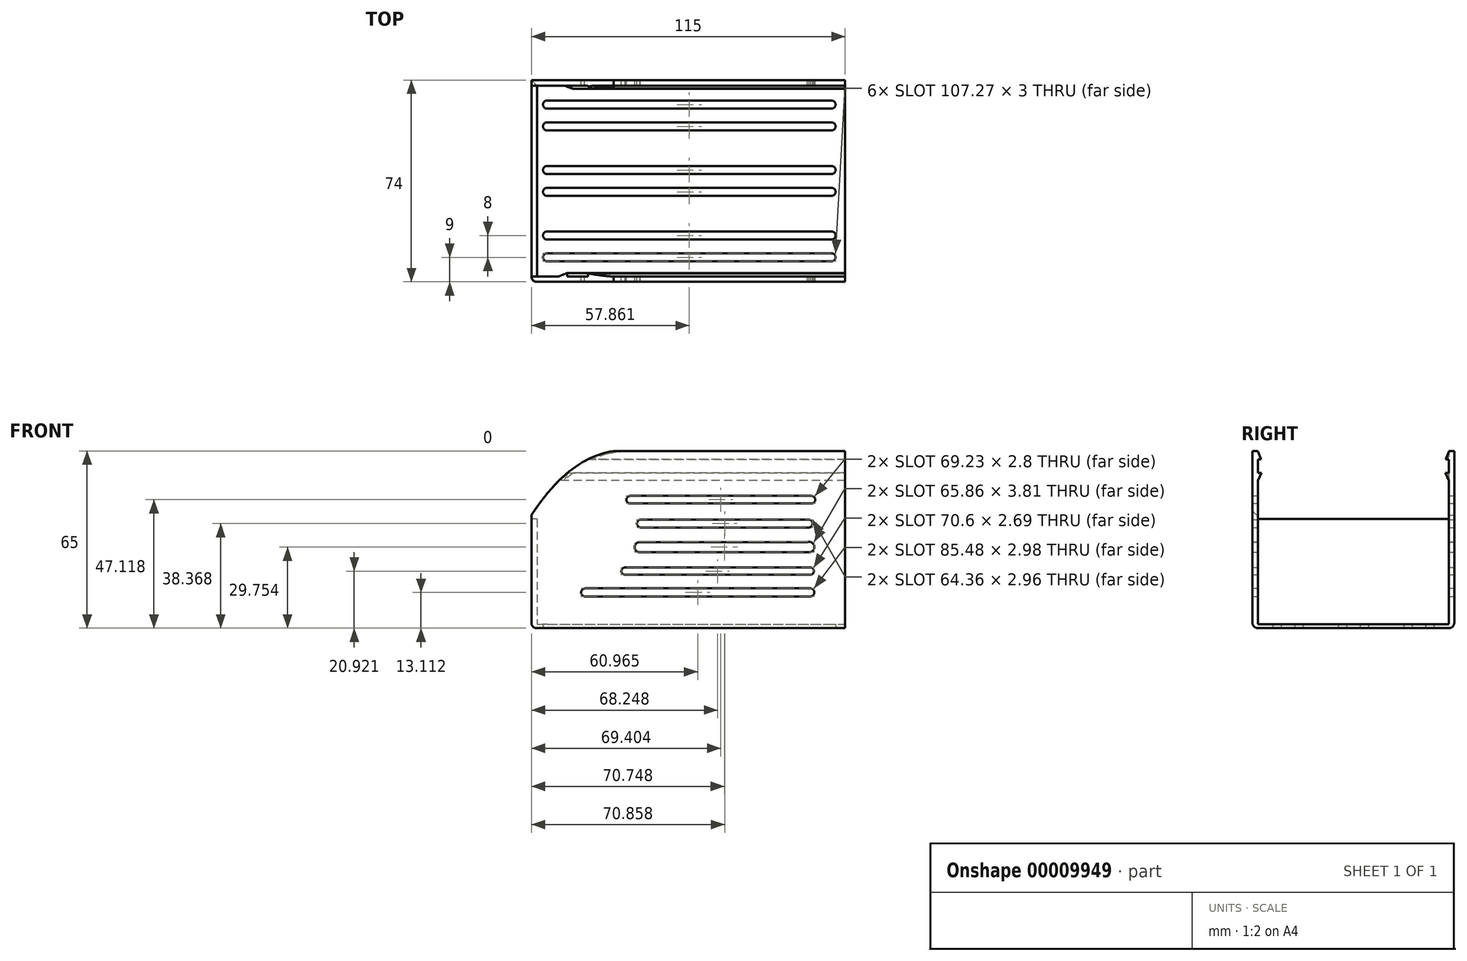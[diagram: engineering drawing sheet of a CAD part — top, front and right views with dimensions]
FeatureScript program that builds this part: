
annotation { "Feature Type Name" : "Feature", "Feature Type Description" : "" }
export const myFeature = defineFeature(function(context is Context, id is Id, definition is map)
    precondition{}
    {
        {
            var Q0;
            Q0=qCreatedBy(makeId("Top.planeOp"),FACE);
            var sketch = newSketch(context, id + "F0", { "sketchPlane" : qUnion([Q0])});
            skLineSegment(sketch, "E0.bottom", {"start": v(0, 0) * mm, "end": v(-115, 0) * mm});
            skLineSegment(sketch, "E0.top", {"start": v(0, -74) * mm, "end": v(-115, -74) * mm});
            skLineSegment(sketch, "E0.left", {"start": v(0, 0) * mm, "end": v(0, -74) * mm});
            skLineSegment(sketch, "E0.right", {"start": v(-115, 0) * mm, "end": v(-115, -74) * mm});
            skLineSegment(sketch, "E1", {"start": v(-113, -2) * mm, "end": v(-113, -72) * mm});
            skPoint(sketch, "E2", {"position": v(-113, -37) * mm});
            skLineSegment(sketch, "E3.bottom", {"start": v(-109.27, -34.5) * mm, "end": v(-5, -34.5) * mm});
            skLineSegment(sketch, "E3.top", {"start": v(-109.27, -31.5) * mm, "end": v(-5, -31.5) * mm});
            skLineSegment(sketch, "E4", {"start": v(-109.27, -26.5) * mm, "end": v(-5, -26.5) * mm});
            skLineSegment(sketch, "E5", {"start": v(-109.27, -15.5) * mm, "end": v(-5, -15.5) * mm});
            skLineSegment(sketch, "E6", {"start": v(-109.27, -18.5) * mm, "end": v(-5, -18.5) * mm});
            skLineSegment(sketch, "E7", {"start": v(-5, -23.5) * mm, "end": v(-109.27, -23.5) * mm});
            skArc(sketch, "E8", {"start": v(-109.27, -31.5) * mm, "mid": v(-110.77, -33) * mm, "end": v(-109.27, -34.5) * mm});
            skArc(sketch, "E9", {"start": v(-109.27, -23.5) * mm, "mid": v(-110.77, -25) * mm, "end": v(-109.27, -26.5) * mm});
            skArc(sketch, "E10", {"start": v(-109.27, -15.5) * mm, "mid": v(-110.77, -17) * mm, "end": v(-109.27, -18.5) * mm});
            skLineSegment(sketch, "E11", {"start": v(-109.27, -10.5) * mm, "end": v(-5, -10.5) * mm});
            skLineSegment(sketch, "E12", {"start": v(-5, -7.5) * mm, "end": v(-109.27, -7.5) * mm});
            skArc(sketch, "E13", {"start": v(-109.27, -7.5) * mm, "mid": v(-110.77, -9) * mm, "end": v(-109.27, -10.5) * mm});
            skArc(sketch, "E14", {"start": v(-5, -10.5) * mm, "mid": v(-3.5, -9) * mm, "end": v(-5, -7.5) * mm});
            skArc(sketch, "E15", {"start": v(-5, -18.5) * mm, "mid": v(-3.5, -17) * mm, "end": v(-5, -15.5) * mm});
            skArc(sketch, "E16", {"start": v(-5, -26.5) * mm, "mid": v(-3.37, -24.85) * mm, "end": v(-5.02, -23.23) * mm});
            skArc(sketch, "E17", {"start": v(-5, -34.5) * mm, "mid": v(-3.5, -33) * mm, "end": v(-5, -31.5) * mm});
            skArc(sketch, "E18.MirrorCS", {"start": v(-5, -55.5) * mm, "mid": v(-3.5, -57) * mm, "end": v(-5, -58.5) * mm});
            skArc(sketch, "E19.MirrorCS", {"start": v(-5, -63.5) * mm, "mid": v(-3.5, -65) * mm, "end": v(-5, -66.5) * mm});
            skArc(sketch, "E20.MirrorCS", {"start": v(-5, -47.5) * mm, "mid": v(-3.37, -49.15) * mm, "end": v(-5.02, -50.77) * mm});
            skArc(sketch, "E21.MirrorCS", {"start": v(-5, -39.5) * mm, "mid": v(-3.5, -41) * mm, "end": v(-5, -42.5) * mm});
            skLineSegment(sketch, "E22.MirrorCS", {"start": v(-5, -50.5) * mm, "end": v(-109.27, -50.5) * mm});
            skLineSegment(sketch, "E23.MirrorCS", {"start": v(-109.27, -47.5) * mm, "end": v(-5, -47.5) * mm});
            skLineSegment(sketch, "E24.MirrorCS", {"start": v(-109.27, -55.5) * mm, "end": v(-5, -55.5) * mm});
            skLineSegment(sketch, "E25.MirrorCS", {"start": v(-109.27, -39.5) * mm, "end": v(-5, -39.5) * mm});
            skArc(sketch, "E26.MirrorCS", {"start": v(-109.27, -42.5) * mm, "mid": v(-110.77, -41) * mm, "end": v(-109.27, -39.5) * mm});
            skLineSegment(sketch, "E27.MirrorCS", {"start": v(-109.27, -58.5) * mm, "end": v(-5, -58.5) * mm});
            skArc(sketch, "E28.MirrorCS", {"start": v(-109.27, -50.5) * mm, "mid": v(-110.77, -49) * mm, "end": v(-109.27, -47.5) * mm});
            skArc(sketch, "E29.MirrorCS", {"start": v(-109.27, -66.5) * mm, "mid": v(-110.77, -65) * mm, "end": v(-109.27, -63.5) * mm});
            skLineSegment(sketch, "E30.MirrorCS", {"start": v(-109.27, -63.5) * mm, "end": v(-5, -63.5) * mm});
            skLineSegment(sketch, "E31.MirrorCS", {"start": v(-5, -66.5) * mm, "end": v(-109.27, -66.5) * mm});
            skLineSegment(sketch, "E32.MirrorCS", {"start": v(-109.27, -42.5) * mm, "end": v(-5, -42.5) * mm});
            skArc(sketch, "E33.MirrorCS", {"start": v(-109.27, -58.5) * mm, "mid": v(-110.77, -57) * mm, "end": v(-109.27, -55.5) * mm});
            skLineSegment(sketch, "E34", {"start": v(-113, -2) * mm, "end": v(0, -2) * mm});
            skLineSegment(sketch, "E35", {"start": v(-113, -72) * mm, "end": v(0, -72) * mm});
            skLineSegment(sketch, "E36", {"start": v(-113, -2) * mm, "end": v(-115, -2) * mm});
            skLineSegment(sketch, "E37", {"start": v(-113, -72) * mm, "end": v(-115, -72) * mm});
            skSolve(sketch);
        }
        {
            var Q0;
            Q0=makeQuery(id+"F0.imprint","IMPRINT",FACE,{"disambiguationData":[TD([[makeQuery(id+"F0.imprint","IMPRINT",EDGE,{"derivedFrom":sQuery(id+"F0.wireOp",EDGE,"E1")}),1.0]])]});
            extrude(context, id + "F1", {"entities" : qUnion([Q0]), "depth" : 1.5 * mm});
        }
        {
            var Q0;
            {var subQ4=sQuery(id+"F0.wireOp",EDGE,"E0.bottom");Q0=makeQuery(id+"F0.imprint","IMPRINT",FACE,{"disambiguationData":[TD([[makeQuery(id+"F0.imprint","IMPRINT",EDGE,{"derivedFrom":subQ4}),1.0]])]});}
            var Q1;
            {var subQ3=sQuery(id+"F0.wireOp",EDGE,"E0.top");Q1=makeQuery(id+"F0.imprint","IMPRINT",FACE,{"disambiguationData":[TD([[makeQuery(id+"F0.imprint","IMPRINT",EDGE,{"derivedFrom":subQ3}),-1.0]])]});}
            extrude(context, id + "F2", {"entities" : qUnion([Q0, Q1]), "operationType" : NewBodyOperationType.ADD, "depth" : 65 * mm});
        }
        {
            var Q0;
            Q0=makeQuery(id+"F0.imprint","IMPRINT",FACE,{"disambiguationData":[TD([[makeQuery(id+"F0.imprint","IMPRINT",EDGE,{"derivedFrom":sQuery(id+"F0.wireOp",EDGE,"E1")}),-1.0]])]});
            extrude(context, id + "F3", {"entities" : qUnion([Q0]), "operationType" : NewBodyOperationType.ADD, "depth" : 40 * mm});
        }
        {
            var Q0;
            Q0=makeQuery(id+"F2.opExtrude","SWEPT_FACE",FACE,{"disambiguationData":[OSD([sQuery(id+"F0.wireOp",EDGE,"E0.bottom")])]});
            var sketch = newSketch(context, id + "F4", { "sketchPlane" : qUnion([Q0])});
            skLineSegment(sketch, "E38.bottom", {"start": v(12.38, 48.52) * mm, "end": v(78.81, 48.52) * mm});
            skLineSegment(sketch, "E38.top", {"start": v(12.38, 45.72) * mm, "end": v(78.81, 45.72) * mm});
            skLineSegment(sketch, "E39.bottom", {"start": v(13.21, 39.85) * mm, "end": v(75.07, 39.85) * mm});
            skLineSegment(sketch, "E39.top", {"start": v(13.45, 36.89) * mm, "end": v(74.84, 36.89) * mm});
            skLineSegment(sketch, "E40.bottom", {"start": v(13.86, 31.55) * mm, "end": v(75.16, 31.55) * mm});
            skLineSegment(sketch, "E40.top", {"start": v(13.2, 27.85) * mm, "end": v(75.33, 27.85) * mm});
            skLineSegment(sketch, "E41.bottom", {"start": v(12.65, 22.27) * mm, "end": v(80.72, 22.27) * mm});
            skLineSegment(sketch, "E41.top", {"start": v(12.8, 19.57) * mm, "end": v(80.7, 19.57) * mm});
            skLineSegment(sketch, "E42.bottom", {"start": v(12.79, 14.6) * mm, "end": v(95.28, 14.6) * mm});
            skLineSegment(sketch, "E42.top", {"start": v(12.6, 11.62) * mm, "end": v(95.52, 11.62) * mm});
            skArc(sketch, "E43", {"start": v(12.38, 48.52) * mm, "mid": v(10.98, 47.12) * mm, "end": v(12.38, 45.72) * mm});
            skArc(sketch, "E44", {"start": v(13.21, 39.85) * mm, "mid": v(11.96, 38.26) * mm, "end": v(13.45, 36.89) * mm});
            skArc(sketch, "E45", {"start": v(13.86, 31.55) * mm, "mid": v(11.32, 30.1) * mm, "end": v(13.2, 27.85) * mm});
            skArc(sketch, "E46", {"start": v(78.81, 45.72) * mm, "mid": v(80.21, 47.12) * mm, "end": v(78.81, 48.52) * mm});
            skArc(sketch, "E47", {"start": v(74.84, 36.89) * mm, "mid": v(76.32, 38.26) * mm, "end": v(75.07, 39.85) * mm});
            skArc(sketch, "E48", {"start": v(75.33, 27.85) * mm, "mid": v(77.18, 29.79) * mm, "end": v(75.16, 31.55) * mm});
            skArc(sketch, "E49", {"start": v(80.7, 19.57) * mm, "mid": v(82.05, 20.91) * mm, "end": v(80.72, 22.27) * mm});
            skArc(sketch, "E50", {"start": v(95.52, 11.62) * mm, "mid": v(96.78, 13.22) * mm, "end": v(95.28, 14.6) * mm});
            skArc(sketch, "E51", {"start": v(12.79, 14.6) * mm, "mid": v(11.3, 13.2) * mm, "end": v(12.6, 11.62) * mm});
            skArc(sketch, "E52", {"start": v(12.65, 22.27) * mm, "mid": v(11.45, 20.85) * mm, "end": v(12.8, 19.57) * mm});
            skSolve(sketch);
        }
        {
            var Q0;
            Q0=makeQuery(id+"F2.opExtrude","SWEPT_FACE",FACE,{"disambiguationData":[OSD([sQuery(id+"F0.wireOp",EDGE,"E0.bottom")])]});
            var sketch = newSketch(context, id + "F5", { "sketchPlane" : qUnion([Q0])});
            skFitSpline(sketch, "E53", {"points": [v(84.32, 65.1) * mm, v(115, 41.5) * mm], "startDerivative": vector(26.25, -4.38) * mm, "endDerivative": vector(34.2, -52.46) * mm});
            skSolve(sketch);
        }
        {
            var Q0;
            Q0=makeQuery(id+"F4.imprint","IMPRINT",FACE,{"disambiguationData":[TD([[makeQuery(id+"F4.imprint","IMPRINT",EDGE,{"derivedFrom":sQuery(id+"F4.wireOp",EDGE,"E38.bottom")}),-1.0]])]});
            var Q1;
            Q1=makeQuery(id+"F4.imprint","IMPRINT",FACE,{"disambiguationData":[TD([[makeQuery(id+"F4.imprint","IMPRINT",EDGE,{"derivedFrom":sQuery(id+"F4.wireOp",EDGE,"E39.bottom")}),-1.0]])]});
            var Q2;
            Q2=makeQuery(id+"F4.imprint","IMPRINT",FACE,{"disambiguationData":[TD([[makeQuery(id+"F4.imprint","IMPRINT",EDGE,{"derivedFrom":sQuery(id+"F4.wireOp",EDGE,"E40.bottom")}),-1.0]])]});
            var Q3;
            Q3=makeQuery(id+"F4.imprint","IMPRINT",FACE,{"disambiguationData":[TD([[makeQuery(id+"F4.imprint","IMPRINT",EDGE,{"derivedFrom":sQuery(id+"F4.wireOp",EDGE,"E41.bottom")}),-1.0]])]});
            var Q4;
            Q4=makeQuery(id+"F4.imprint","IMPRINT",FACE,{"disambiguationData":[TD([[makeQuery(id+"F4.imprint","IMPRINT",EDGE,{"derivedFrom":sQuery(id+"F4.wireOp",EDGE,"E42.bottom")}),-1.0]])]});
            var Q5;
            Q5=makeQuery(id+"F4.imprint","IMPRINT",FACE,{"disambiguationData":[TD([[makeQuery(id+"F4.imprint","IMPRINT",EDGE,{"derivedFrom":sQuery(id+"F4.wireOp",EDGE,"3dbdf3a3-7501-48f6-ba3e-7b58e3537750.left")}),1.0]])]});
            var Q6;
            Q6=makeQuery(id+"F4.imprint","IMPRINT",FACE,{"disambiguationData":[TD([[makeQuery(id+"F4.imprint","IMPRINT",EDGE,{"derivedFrom":sQuery(id+"F4.wireOp",EDGE,"3dbdf3a3-7501-48f6-ba3e-7b58e3537750.bottom")}),1.0]])]});
            extrude(context, id + "F6", {"entities" : qUnion([Q0, Q1, Q2, Q3, Q4, Q5, Q6]), "operationType" : NewBodyOperationType.REMOVE, "oppositeDirection" : true, "depth" : 80.15 * mm});
        }
        {
            var Q0;
            Q0=makeQuery(id+"F2.opExtrude","CAP_EDGE",EDGE,{"disambiguationData":[OSD([sQuery(id+"F0.wireOp",EDGE,"E0.bottom")])],"isStart":true});
            var Q1;
            {var subQ0=sQuery(id+"F0.wireOp",EDGE,"E0.right");Q1=makeQuery(id+"F3.boolean.opBoolean","MERGE",EDGE,{"derivedFrom":[makeQuery(id+"F2.opExtrude","CAP_EDGE",EDGE,{"disambiguationData":[OSD([subQ0]),TDD([makeQuery(id+"F0.imprint","IMPRINT",EDGE,{"disambiguationData":[TD([[makeQuery(id+"F0.imprint","INTERSECT",VERTEX,{"derivedFrom":[sQuery(id+"F0.wireOp",EDGE,"E0.bottom"),subQ0]}),-1.0]])],"derivedFrom":subQ0})])],"isStart":true}),makeQuery(id+"F2.opExtrude","CAP_EDGE",EDGE,{"disambiguationData":[OSD([subQ0]),TDD([makeQuery(id+"F0.imprint","IMPRINT",EDGE,{"disambiguationData":[TD([[makeQuery(id+"F0.imprint","INTERSECT",VERTEX,{"derivedFrom":[sQuery(id+"F0.wireOp",EDGE,"E0.top"),subQ0]}),1.0]])],"derivedFrom":subQ0})])],"isStart":true}),makeQuery(id+"F3.opExtrude","CAP_EDGE",EDGE,{"disambiguationData":[OSD([subQ0])],"isStart":true})]});}
            fillet(context, id + "F7", {"entities" : qUnion([Q0, Q1]), "radius" : 2 * mm, "tangentPropagation" : true, "allowEdgeOverflow" : false});
        }
        {
            var Q0;
            Q0=makeQuery(id+"F2.opExtrude","CAP_EDGE",EDGE,{"disambiguationData":[OSD([sQuery(id+"F0.wireOp",EDGE,"E0.top")])],"isStart":true});
            var Q1;
            Q1=makeQuery(id+"F1.opExtrude","CAP_EDGE",EDGE,{"disambiguationData":[OSD([sQuery(id+"F0.wireOp",EDGE,"E35")])],"isStart":false});
            var Q2;
            Q2=makeQuery(id+"F1.opExtrude","CAP_EDGE",EDGE,{"disambiguationData":[OSD([sQuery(id+"F0.wireOp",EDGE,"E34")])],"isStart":false});
            var Q3;
            Q3=makeQuery(id+"F1.opExtrude","CAP_EDGE",EDGE,{"disambiguationData":[OSD([sQuery(id+"F0.wireOp",EDGE,"E1")])],"isStart":false});
            fillet(context, id + "F8", {"entities" : qUnion([Q0, Q1, Q2, Q3]), "radius" : 2 * mm, "tangentPropagation" : true, "allowEdgeOverflow" : false});
        }
        {
            var Q0;
            {var subQ0=sQuery(id+"F0.wireOp",EDGE,"E0.right");Q0=makeQuery(id+"F3.boolean.opBoolean","MERGE",FACE,{"derivedFrom":[makeQuery(id+"F2.opExtrude","SWEPT_FACE",FACE,{"disambiguationData":[OSD([subQ0]),TDD([makeQuery(id+"F0.imprint","IMPRINT",EDGE,{"disambiguationData":[TD([[makeQuery(id+"F0.imprint","INTERSECT",VERTEX,{"derivedFrom":[sQuery(id+"F0.wireOp",EDGE,"E0.bottom"),subQ0]}),-1.0]])],"derivedFrom":subQ0})])]}),makeQuery(id+"F2.opExtrude","SWEPT_FACE",FACE,{"disambiguationData":[OSD([subQ0]),TDD([makeQuery(id+"F0.imprint","IMPRINT",EDGE,{"disambiguationData":[TD([[makeQuery(id+"F0.imprint","INTERSECT",VERTEX,{"derivedFrom":[sQuery(id+"F0.wireOp",EDGE,"E0.top"),subQ0]}),1.0]])],"derivedFrom":subQ0})])]}),makeQuery(id+"F3.opExtrude","SWEPT_FACE",FACE,{"disambiguationData":[OSD([subQ0])]})]});}
            var sketch = newSketch(context, id + "F9", { "sketchPlane" : qUnion([Q0])});
            skSolve(sketch);
        }
        {
            var Q0;
            {var subQ0=sQuery(id+"F0.wireOp",EDGE,"E0.right");Q0=makeQuery(id+"F9.imprint","IMPRINT",FACE,{"disambiguationData":[TD([[makeQuery(id+"F9.imprint","IMPRINT",EDGE,{"derivedFrom":makeQuery(id+"F3.opExtrude","CAP_EDGE",EDGE,{"disambiguationData":[OSD([subQ0])],"isStart":false})}),-1.0]])]});}
            var sketch = newSketch(context, id + "F10", { "sketchPlane" : qUnion([Q0])});
            skLineSegment(sketch, "E54", {"start": v(1.24, 61.9) * mm, "end": v(1.24, 56.9) * mm});
            skLineSegment(sketch, "E55", {"start": v(1.24, 61.9) * mm, "end": v(3.1, 61.9) * mm});
            skLineSegment(sketch, "E56", {"start": v(3.1, 61.9) * mm, "end": v(1.95, 64.88) * mm});
            skLineSegment(sketch, "E57", {"start": v(1.24, 56.9) * mm, "end": v(3.24, 56.9) * mm});
            skLineSegment(sketch, "E58", {"start": v(3.24, 56.9) * mm, "end": v(1.89, 53.89) * mm});
            skPoint(sketch, "E59", {"position": v(-20.95, 35.18) * mm});
            skLineSegment(sketch, "E60", {"start": v(73.98, 12.5) * mm, "end": v(0, 12.5) * mm});
            skPoint(sketch, "E61", {"position": v(37, 12.5) * mm});
            skLineSegment(sketch, "E62", {"start": v(37, 12.5) * mm, "end": v(37, 50.28) * mm});
            skLineSegment(sketch, "E63.MirrorCS", {"start": v(70.87, 61.9) * mm, "end": v(72.03, 64.88) * mm});
            skLineSegment(sketch, "E64.MirrorCS", {"start": v(72.74, 61.9) * mm, "end": v(70.87, 61.9) * mm});
            skLineSegment(sketch, "E65.MirrorCS", {"start": v(72.74, 61.9) * mm, "end": v(72.74, 56.9) * mm});
            skLineSegment(sketch, "E66.MirrorCS", {"start": v(72.74, 56.9) * mm, "end": v(70.74, 56.9) * mm});
            skLineSegment(sketch, "E67.MirrorCS", {"start": v(70.74, 56.9) * mm, "end": v(72.1, 53.89) * mm});
            skLineSegment(sketch, "E68", {"start": v(1.24, 61.9) * mm, "end": v(1.95, 64.88) * mm});
            skLineSegment(sketch, "E69", {"start": v(1.24, 56.9) * mm, "end": v(1.89, 53.89) * mm});
            skLineSegment(sketch, "E70", {"start": v(72.03, 64.88) * mm, "end": v(72.74, 61.9) * mm});
            skLineSegment(sketch, "E71", {"start": v(72.74, 56.9) * mm, "end": v(72.1, 53.89) * mm});
            skSolve(sketch);
        }
        {
            var Q0;
            Q0=qSketchRegion(id+"F10",true);
            var Q1;
            Q1=makeQuery(id+"F10.imprint","IMPRINT",FACE,{"disambiguationData":[TD([[makeQuery(id+"F10.imprint","IMPRINT",EDGE,{"derivedFrom":sQuery(id+"F10.wireOp",EDGE,"E57")}),-1.0]])]});
            extrude(context, id + "F11", {"entities" : qUnion([Q0, Q1]), "operationType" : NewBodyOperationType.ADD, "oppositeDirection" : true, "depth" : 115 * mm});
        }
        {
            var Q0;
            {var subQ2=sQuery(id+"F5.wireOp",EDGE,"30a2cea3-d1ab-40d1-a56c-51a4d7a3f610");Q0=makeQuery(id+"F5.imprint","IMPRINT",FACE,{"disambiguationData":[TD([[makeQuery(id+"F5.imprint","IMPRINT",EDGE,{"derivedFrom":subQ2}),1.0]])]});}
            var Q1;
            {var subQ1=sQuery(id+"F5.wireOp",EDGE,"E53");Q1=makeQuery(id+"F5.imprint","IMPRINT",FACE,{"disambiguationData":[TD([[makeQuery(id+"F5.imprint","IMPRINT",EDGE,{"derivedFrom":subQ1}),1.0]])]});}
            extrude(context, id + "F12", {"entities" : qUnion([Q0, Q1]), "operationType" : NewBodyOperationType.REMOVE, "endBound" : BoundingType.THROUGH_ALL, "oppositeDirection" : true, "depth" : 4 * mm});
        }
        {
            var Q0;
            Q0=makeQuery(id+"F12.boolean.opBoolean","INTERSECT",EDGE,{"derivedFrom":[makeQuery(id+"F11.opExtrude","SWEPT_FACE",FACE,{"disambiguationData":[OSD([sQuery(id+"F10.wireOp",EDGE,"E58")])]}),makeQuery(id+"F12.opExtrude","SWEPT_FACE",FACE,{"disambiguationData":[OSD([sQuery(id+"F5.wireOp",EDGE,"E53")])]})]});
            chamfer(context, id + "F13", {"entities" : qUnion([Q0]), "width" : 1 * mm, "tangentPropagation" : true});
        }
        {
            var Q0;
            Q0=makeQuery(id+"F12.boolean.opBoolean","INTERSECT",EDGE,{"derivedFrom":[makeQuery(id+"F11.opExtrude","SWEPT_FACE",FACE,{"disambiguationData":[OSD([sQuery(id+"F10.wireOp",EDGE,"E56")])]}),makeQuery(id+"F12.opExtrude","SWEPT_FACE",FACE,{"disambiguationData":[OSD([sQuery(id+"F5.wireOp",EDGE,"E53")])]})]});
            chamfer(context, id + "F14", {"entities" : qUnion([Q0]), "width" : 1 * mm, "tangentPropagation" : true});
        }
    });
